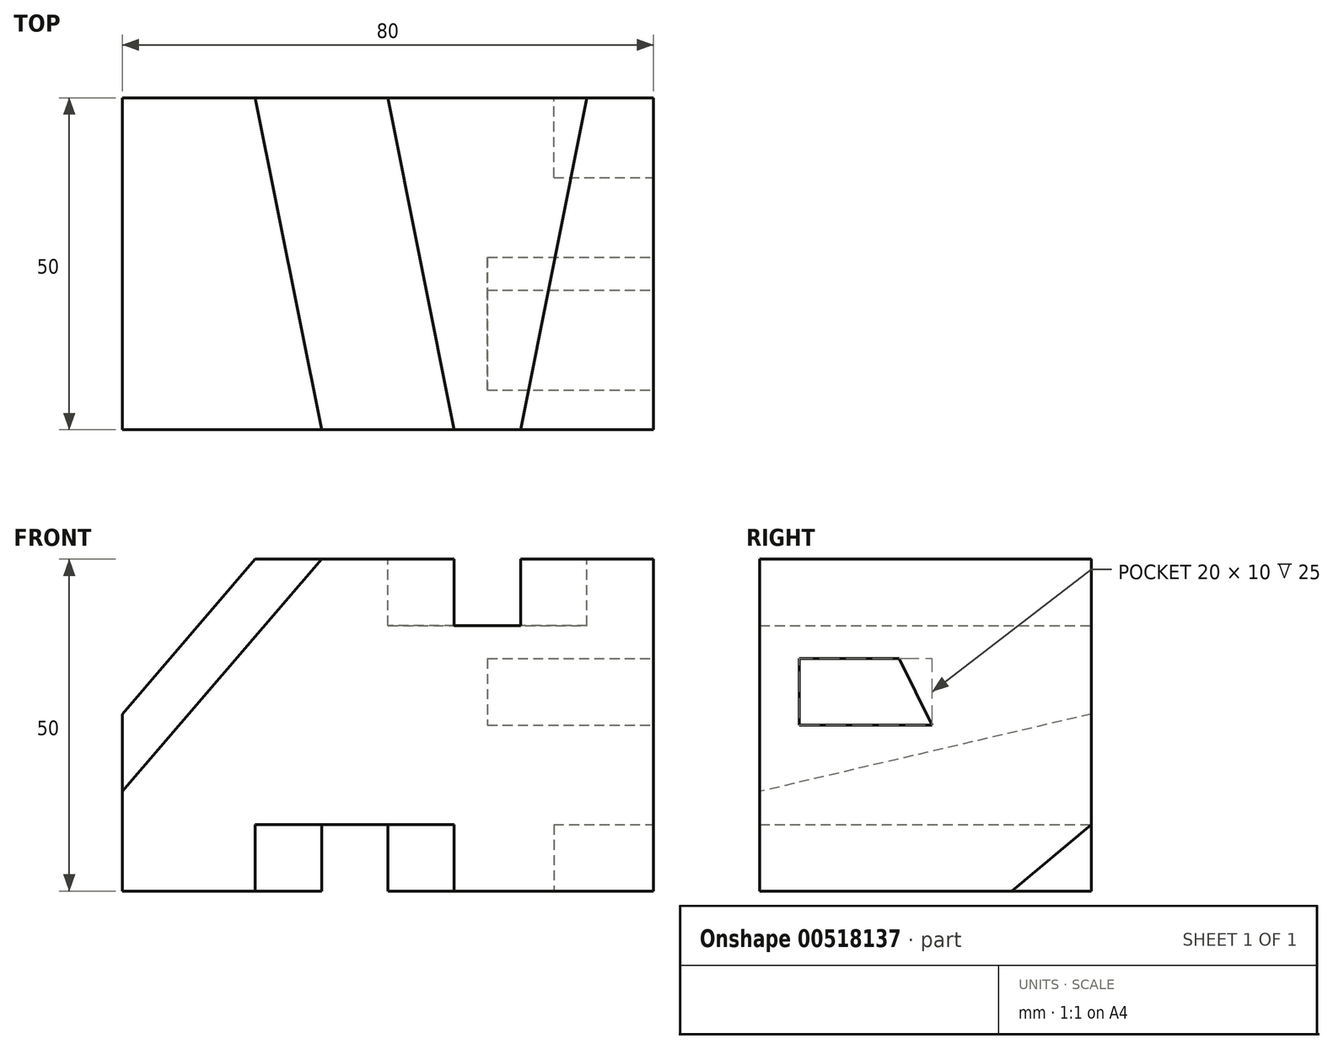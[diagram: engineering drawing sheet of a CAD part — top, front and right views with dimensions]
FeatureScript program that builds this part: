
annotation { "Feature Type Name" : "Feature", "Feature Type Description" : "" }
export const myFeature = defineFeature(function(context is Context, id is Id, definition is map)
    precondition{}
    {
        {
            var Q0;
            Q0=qCreatedBy(makeId("Top.planeOp"),FACE);
            var sketch = newSketch(context, id + "F0", { "sketchPlane" : qUnion([Q0])});
            skLineSegment(sketch, "E0.bottom", {"start": v(0, 0) * mm, "end": v(80, 0) * mm});
            skLineSegment(sketch, "E0.top", {"start": v(0, 50) * mm, "end": v(80, 50) * mm});
            skLineSegment(sketch, "E0.left", {"start": v(0, 0) * mm, "end": v(0, 50) * mm});
            skLineSegment(sketch, "E0.right", {"start": v(80, 0) * mm, "end": v(80, 50) * mm});
            skSolve(sketch);
        }
        {
            var Q0;
            Q0 = qSketchRegion(id + "F0", true);
            extrude(context, id + "F1", {"entities" : qUnion([Q0]), "depth" : 50 * mm, "offsetDistance" : 25 * mm});
        }
        {
            var Q0;
            Q0=makeQuery(id+"F1.opExtrude","SWEPT_FACE",FACE,{"disambiguationData":[OSD([sQuery(id+"F0.wireOp",EDGE,"E0.bottom")])]});
            var sketch = newSketch(context, id + "F2", { "sketchPlane" : qUnion([Q0])});
            skLineSegment(sketch, "E1", {"start": v(0, 0) * mm, "end": v(0, 15) * mm});
            skLineSegment(sketch, "E2", {"start": v(0, 15) * mm, "end": v(30, 50) * mm});
            skLineSegment(sketch, "E3", {"start": v(30, 50) * mm, "end": v(0, 50) * mm});
            skSolve(sketch);
        }
        {
            var Q0;
            Q0=makeQuery(id+"F1.opExtrude","CAP_FACE",FACE,{"disambiguationData":[OSD([sQuery(id+"F0.wireOp",EDGE,"E0.bottom"),sQuery(id+"F0.wireOp",EDGE,"E0.top"),sQuery(id+"F0.wireOp",EDGE,"E0.left"),sQuery(id+"F0.wireOp",EDGE,"E0.right")])],"isStart":false});
            var sketch = newSketch(context, id + "F3", { "sketchPlane" : qUnion([Q0])});
            skLineSegment(sketch, "E4", {"start": v(0, 0) * mm, "end": v(30, 0) * mm});
            skLineSegment(sketch, "E5", {"start": v(30, 0) * mm, "end": v(20, 50) * mm});
            skLineSegment(sketch, "E6", {"start": v(20, 50) * mm, "end": v(0, 50) * mm});
            skSolve(sketch);
        }
        {
            var Q0;
            {var subQ0=sQuery(id+"F2.wireOp",EDGE,"E2");Q0=makeQuery(id+"F2.imprint","IMPRINT",FACE,{"disambiguationData":[TD([[makeQuery(id+"F2.imprint","IMPRINT",EDGE,{"derivedFrom":subQ0}),1.0]])]});}
            var Q1;
            Q1=sQuery(id+"F3.wireOp",EDGE,"E5");
            sweep(context, id + "F4", {"operationType" : NewBodyOperationType.REMOVE, "profiles" : qUnion([Q0]), "path" : qUnion([Q1])});
        }
        {
            var Q0;
            Q0=makeQuery(id+"F1.opExtrude","CAP_FACE",FACE,{"disambiguationData":[OSD([sQuery(id+"F0.wireOp",EDGE,"E0.bottom"),sQuery(id+"F0.wireOp",EDGE,"E0.top"),sQuery(id+"F0.wireOp",EDGE,"E0.left"),sQuery(id+"F0.wireOp",EDGE,"E0.right")])],"isStart":true});
            var sketch = newSketch(context, id + "F5", { "sketchPlane" : qUnion([Q0])});
            skLineSegment(sketch, "E7", {"start": v(0, 0) * mm, "end": v(20, 0) * mm});
            skLineSegment(sketch, "E8", {"start": v(20, 0) * mm, "end": v(50, 0) * mm});
            skLineSegment(sketch, "E9", {"start": v(50, 0) * mm, "end": v(40, -50) * mm});
            skLineSegment(sketch, "E10", {"start": v(40, -50) * mm, "end": v(30, -50) * mm});
            skLineSegment(sketch, "E11", {"start": v(30, -50) * mm, "end": v(20, 0) * mm});
            skSolve(sketch);
        }
        {
            var Q0;
            Q0 = qSketchRegion(id + "F5", true);
            extrude(context, id + "F6", {"entities" : qUnion([Q0]), "operationType" : NewBodyOperationType.REMOVE, "oppositeDirection" : true, "depth" : 10 * mm, "offsetDistance" : 25 * mm});
        }
        {
            var Q0;
            Q0=makeQuery(id+"F1.opExtrude","SWEPT_FACE",FACE,{"disambiguationData":[OSD([sQuery(id+"F0.wireOp",EDGE,"E0.right")])]});
            var sketch = newSketch(context, id + "F7", { "sketchPlane" : qUnion([Q0])});
            skLineSegment(sketch, "E12", {"start": v(50, 0) * mm, "end": v(38, 0) * mm});
            skLineSegment(sketch, "E13", {"start": v(38, 0) * mm, "end": v(50, 10) * mm});
            skLineSegment(sketch, "E14", {"start": v(50, 10) * mm, "end": v(50, 0) * mm});
            skSolve(sketch);
        }
        {
            var Q0;
            Q0 = qSketchRegion(id + "F7", true);
            extrude(context, id + "F8", {"entities" : qUnion([Q0]), "operationType" : NewBodyOperationType.REMOVE, "oppositeDirection" : true, "depth" : 15 * mm, "offsetDistance" : 25 * mm});
        }
        {
            var Q0;
            Q0=makeQuery(id+"F1.opExtrude","SWEPT_FACE",FACE,{"disambiguationData":[OSD([sQuery(id+"F0.wireOp",EDGE,"E0.right")])]});
            var sketch = newSketch(context, id + "F9", { "sketchPlane" : qUnion([Q0])});
            skLineSegment(sketch, "E15", {"start": v(6, 35) * mm, "end": v(6, 25) * mm});
            skLineSegment(sketch, "E16", {"start": v(6, 25) * mm, "end": v(26, 25) * mm});
            skLineSegment(sketch, "E17", {"start": v(26, 25) * mm, "end": v(21, 35) * mm});
            skLineSegment(sketch, "E18", {"start": v(21, 35) * mm, "end": v(6, 35) * mm});
            skSolve(sketch);
        }
        {
            var Q0;
            Q0=makeQuery(id+"F9.imprint","IMPRINT",FACE,{"disambiguationData":[TD([[makeQuery(id+"F9.imprint","IMPRINT",EDGE,{"derivedFrom":sQuery(id+"F9.wireOp",EDGE,"E15")}),1.0]])]});
            extrude(context, id + "F10", {"entities" : qUnion([Q0]), "operationType" : NewBodyOperationType.REMOVE, "oppositeDirection" : true, "depth" : 25 * mm, "offsetDistance" : 25 * mm});
        }
        {
            var Q0;
            Q0=makeQuery(id+"F1.opExtrude","CAP_FACE",FACE,{"disambiguationData":[OSD([sQuery(id+"F0.wireOp",EDGE,"E0.bottom"),sQuery(id+"F0.wireOp",EDGE,"E0.top"),sQuery(id+"F0.wireOp",EDGE,"E0.left"),sQuery(id+"F0.wireOp",EDGE,"E0.right")])],"isStart":false});
            var sketch = newSketch(context, id + "F11", { "sketchPlane" : qUnion([Q0])});
            skLineSegment(sketch, "E19", {"start": v(0, 0) * mm, "end": v(50, 0) * mm});
            skLineSegment(sketch, "E20", {"start": v(50, 0) * mm, "end": v(40, 50) * mm});
            skLineSegment(sketch, "E21", {"start": v(40, 50) * mm, "end": v(0, 50) * mm});
            skLineSegment(sketch, "E22", {"start": v(0, 50) * mm, "end": v(70, 50) * mm});
            skLineSegment(sketch, "E23", {"start": v(70, 50) * mm, "end": v(60, 0) * mm});
            skLineSegment(sketch, "E24", {"start": v(60, 0) * mm, "end": v(50, 0) * mm});
            skSolve(sketch);
        }
        {
            var Q0;
            Q0 = qSketchRegion(id + "F11", true);
            extrude(context, id + "F12", {"entities" : qUnion([Q0]), "operationType" : NewBodyOperationType.REMOVE, "oppositeDirection" : true, "depth" : 10 * mm, "offsetDistance" : 25 * mm});
        }
    });
